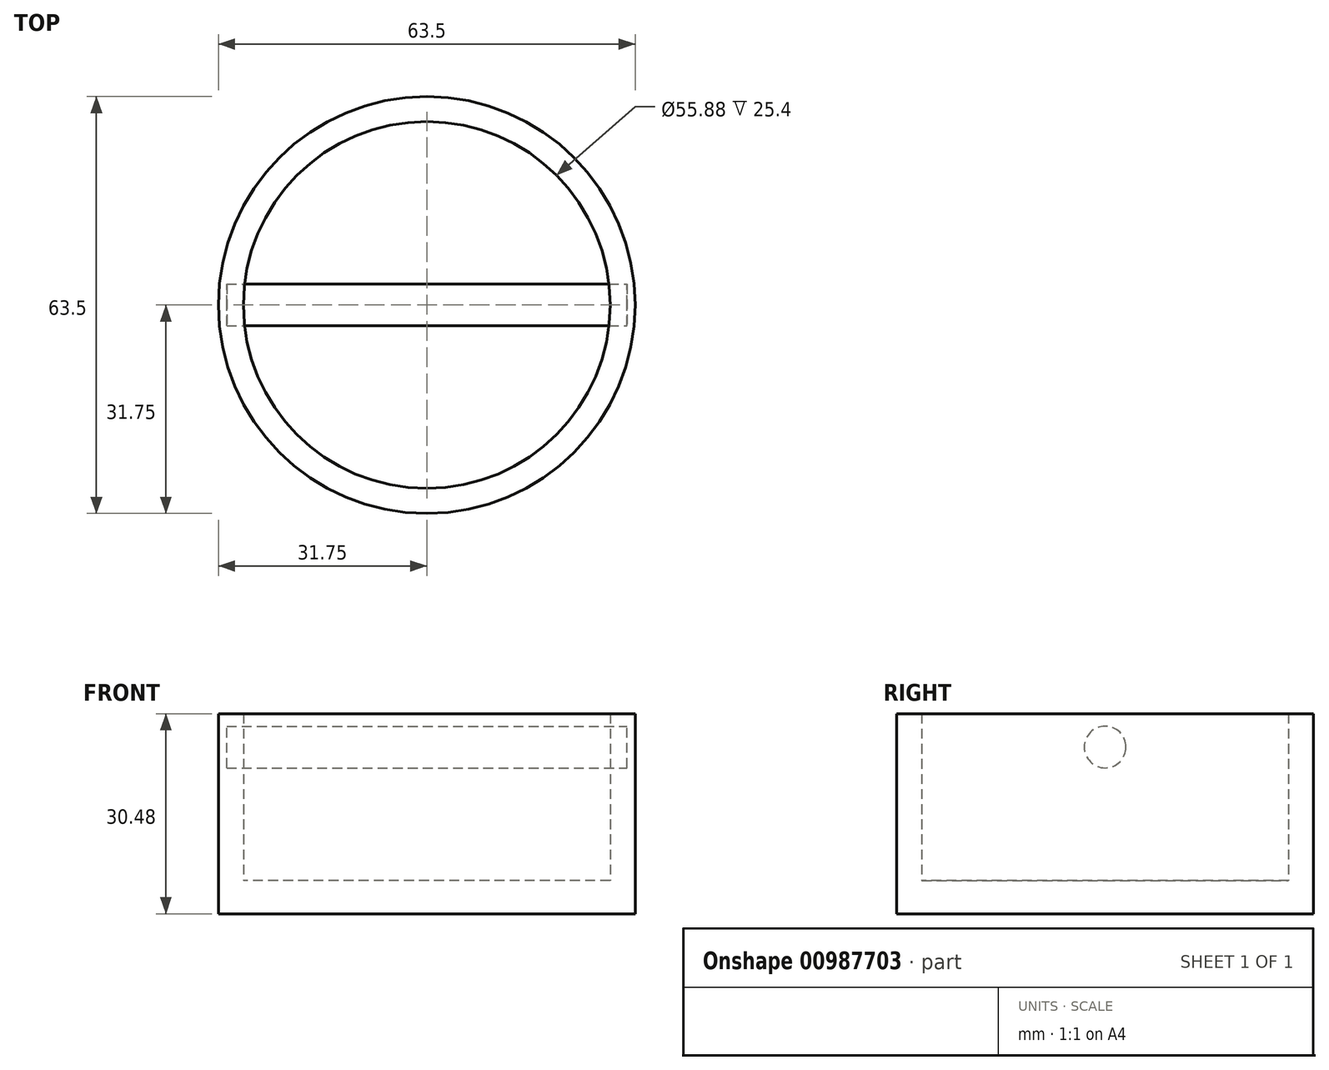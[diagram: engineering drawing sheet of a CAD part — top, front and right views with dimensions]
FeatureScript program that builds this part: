
annotation { "Feature Type Name" : "Feature", "Feature Type Description" : "" }
export const myFeature = defineFeature(function(context is Context, id is Id, definition is map)
    precondition{}
    {
        {
            var Q0;
            Q0=qCreatedBy(makeId("Top.planeOp"),FACE);
            var sketch = newSketch(context, id + "F0", { "sketchPlane" : qUnion([Q0])});
            skCircle(sketch, "E0", {"center": v(0, 0) * mm, "radius": 27.94 * mm});
            skCircle(sketch, "E1", {"center": v(0, 0) * mm, "radius": 31.75 * mm});
            skSolve(sketch);
        }
        {
            var Q0;
            Q0=makeQuery(id+"F0.imprint","IMPRINT",FACE,{"disambiguationData":[TD([[makeQuery(id+"F0.imprint","IMPRINT",EDGE,{"derivedFrom":sQuery(id+"F0.wireOp",EDGE,"E0")}),-1.0]])]});
            extrude(context, id + "F1", {"entities" : qUnion([Q0]), "depth" : 25.4 * mm, "offsetDistance" : 25.4 * mm});
        }
        {
            var Q0;
            Q0=qCreatedBy(makeId("Right.planeOp"),FACE);
            var sketch = newSketch(context, id + "F2", { "sketchPlane" : qUnion([Q0])});
            skCircle(sketch, "E2", {"center": v(0, 20.32) * mm, "radius": 3.18 * mm});
            skSolve(sketch);
        }
        {
            var Q0;
            Q0=makeQuery(id+"F2.imprint","IMPRINT",FACE,{"disambiguationData":[TD([[makeQuery(id+"F2.imprint","IMPRINT",EDGE,{"derivedFrom":sQuery(id+"F2.wireOp",EDGE,"E2")}),1.0]])]});
            extrude(context, id + "F3", {"entities" : qUnion([Q0]), "oppositeDirection" : true, "depth" : 30.48 * mm, "offsetDistance" : 25.4 * mm, "hasSecondDirection" : true, "secondDirectionOppositeDirection" : false, "secondDirectionDepth" : 30.48 * mm});
        }
        {
            var Q0;
            Q0=qCreatedBy(makeId("Top.planeOp"),FACE);
            var sketch = newSketch(context, id + "F4", { "sketchPlane" : qUnion([Q0])});
            skCircle(sketch, "E3", {"center": v(0, 0) * mm, "radius": 31.75 * mm});
            skSolve(sketch);
        }
        {
            var Q0;
            Q0=makeQuery(id+"F4.imprint","IMPRINT",FACE,{"disambiguationData":[TD([[makeQuery(id+"F4.imprint","IMPRINT",EDGE,{"derivedFrom":sQuery(id+"F4.wireOp",EDGE,"E3")}),1.0]])]});
            extrude(context, id + "F5", {"entities" : qUnion([Q0]), "operationType" : NewBodyOperationType.ADD, "oppositeDirection" : true, "depth" : 5.08 * mm, "offsetDistance" : 25.4 * mm});
        }
    });
